# Revit family: LRTZ
name_source: partatom
category: Lighting Fixtures
units: mm (PartAtom-declared; Revit-internal decimal feet)

## family parameters
Always vertical = Yes
Cut with Voids When Loaded = No
Host = Ceiling
Light Source = Yes
OmniClass Number = 23.80.70.11.14.17
OmniClass Title = Direct/Indirect
Part Type = Normal
Room Calculation Point = No
Round Connector Dimension = Use Diameter
Shared = No

## types (7) — shared parameters
Assembly Code = D5020200
Color Filter = 16777215
Description = LED Troffer Dished Lensed
Dimming Lamp Color Temperature Shift = <None>
Emit Shape Visible in Rendering = No
Housing Finish = Metal - Viscor - White
Lamp = LED
Lens Finish = Polycarbonate - Viscor - Frosted
Manufacturer = VISIONEERING by VISCOR
Model = LRTZ
Tilt Angle = 90.00°
URL = https://www.viscor.com
Voltage = 120 V

## per-type parameters (varying)
| type | Apparent Load | Emit from Rectangle Length | Emit from Rectangle Width | Lamp Wattage | Length | Photometric Web File | Reflector Width | Width |
| LRTZ2X2-LED840K020LUNV | 21 VA | 1' - 11 3/4" | 1' - 11 3/4" | 21 VA | 1' - 11 3/4" | LRTZ2x2-LED840K020LUNV-G001324.IES | 0' - 11 7/8" | 1' - 11 3/4" |
| LRTZ2x4-LED840K040LUNV | 29 VA | 3' - 11 3/4" | 1' - 11 3/4" | 29 VA | 3' - 11 3/4" | LRTZ2x4-LED840K040LUNV-G002102.IES | 0' - 11 7/8" | 1' - 11 3/4" |
| LRTZ2X2-LED840K032LUNV | 30 VA | 1' - 11 3/4" | 1' - 11 3/4" | 30 VA | 1' - 11 3/4" | LRTZ2x2-LED840K032LUNV-G001317.IES | 0' - 11 7/8" | 1' - 11 3/4" |
| LRTZ2X4-LED840K050LUNV | 36 VA | 3' - 11 3/4" | 1' - 11 3/4" | 36 VA | 3' - 11 3/4" | LRTZ2x4-LED840K050LUNV-G002152.IES | 0' - 11 7/8" | 1' - 11 3/4" |
| LRTZ1X4-LED840K040LUNV | 29 VA | 3' - 11 3/4" | 0' - 11 3/4" | 29 VA | 3' - 11 3/4" | LRTZ1x4-LED840K040LUNV-G001815.IES | 0' - 5 7/8" | 0' - 11 3/4" |
| LRTZ1X4-LED840K050LUNV | 36 VA | 3' - 11 3/4" | 0' - 11 3/4" | 36 VA | 3' - 11 3/4" | LRTZ1x4-LED840K050LUNV.ies | 0' - 5 7/8" | 0' - 11 3/4" |
| LRTZ30X30-LED840K032LUNV | 30 VA | 2' - 5 3/4" | 2' - 5 3/4" | 30 VA | 2' - 5 3/4" | LRTZ30x30-LED835K032LUNV.IES | 1' - 2 7/8" | 2' - 5 3/4" |

## geometry (parser evidence)
native form markers: Sweep x4
no freeform markers — native parametric forms only
